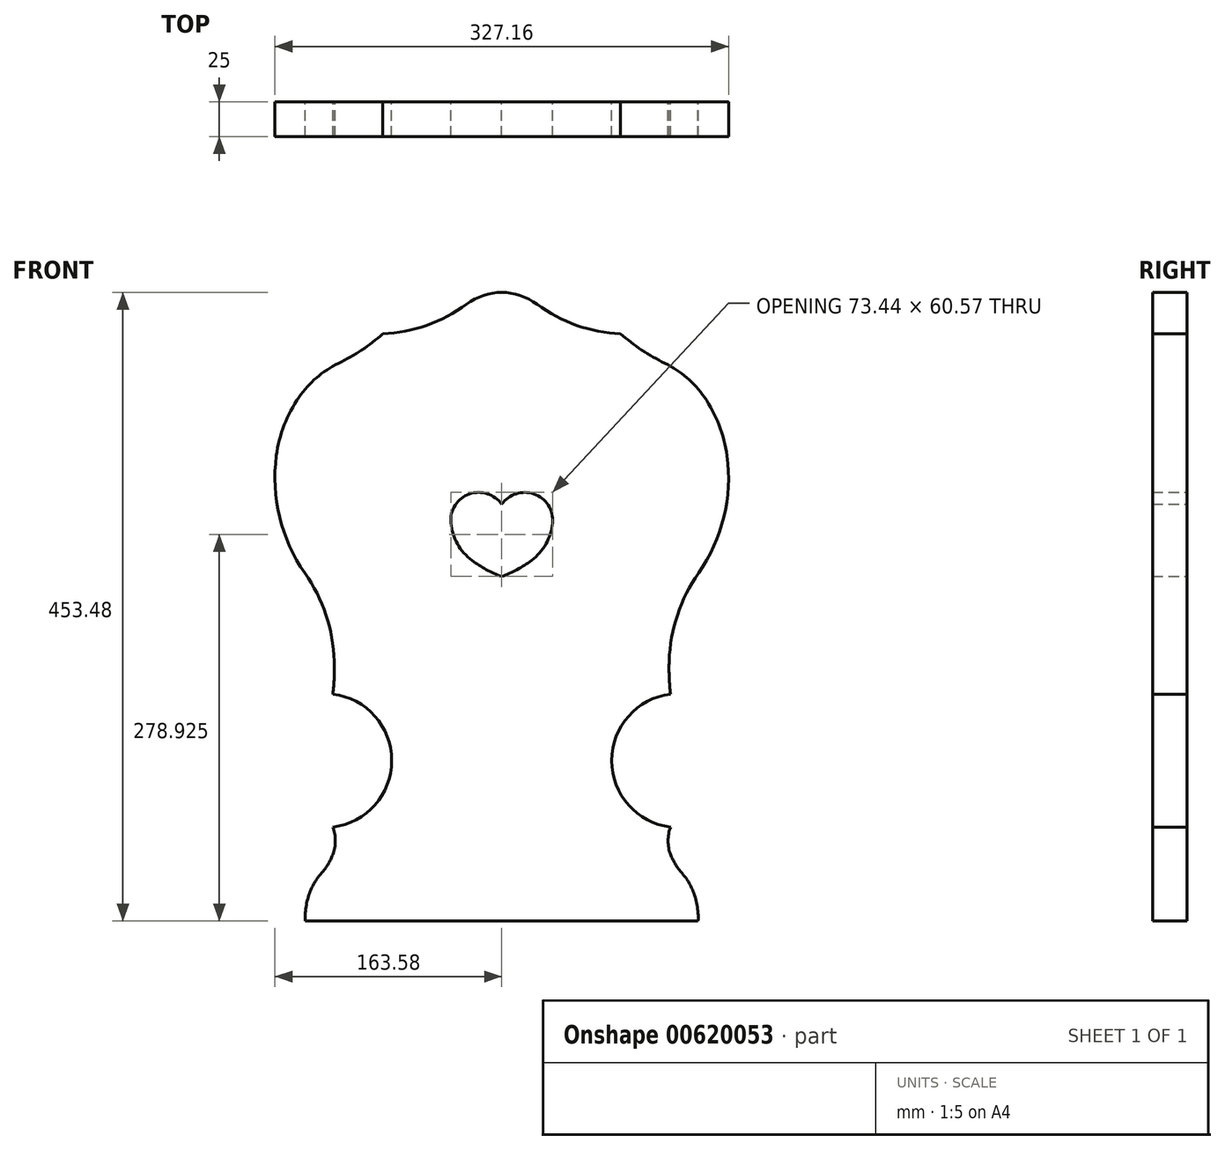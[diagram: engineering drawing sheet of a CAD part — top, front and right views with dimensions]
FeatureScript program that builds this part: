
annotation { "Feature Type Name" : "Feature", "Feature Type Description" : "" }
export const myFeature = defineFeature(function(context is Context, id is Id, definition is map)
    precondition{}
    {
        {
            var Q0;
            Q0=qCreatedBy(makeId("Front.planeOp"),FACE);
            var sketch = newSketch(context, id + "F0", { "sketchPlane" : qUnion([Q0])});
            skLineSegment(sketch, "E0", {"start": v(166.72, 456.5) * mm, "end": v(166.72, 0) * mm, "construction": true});
            skArc(sketch, "E1", {"start": v(81.01, 423.75) * mm, "mid": v(112.75, 429.77) * mm, "end": v(141.24, 445) * mm});
            skArc(sketch, "E2", {"start": v(4.2, 335.64) * mm, "mid": v(6.53, 291.46) * mm, "end": v(24.73, 251.14) * mm});
            skArc(sketch, "E3", {"start": v(24.73, 251.14) * mm, "mid": v(39.95, 220.9) * mm, "end": v(45.97, 187.6) * mm});
            skArc(sketch, "E4", {"start": v(45.97, 187.6) * mm, "mid": v(45.91, 175.63) * mm, "end": v(44.88, 163.7) * mm});
            skArc(sketch, "E5", {"start": v(44.88, 67.88) * mm, "mid": v(87.38, 115.8) * mm, "end": v(44.88, 163.7) * mm});
            skArc(sketch, "E6", {"start": v(4.2, 335.64) * mm, "mid": v(9.88, 357.82) * mm, "end": v(20.59, 378.06) * mm});
            skArc(sketch, "E7", {"start": v(20.59, 378.06) * mm, "mid": v(33.22, 392.07) * mm, "end": v(49, 402.4) * mm});
            skArc(sketch, "E8", {"start": v(49, 402.4) * mm, "mid": v(65.74, 411.97) * mm, "end": v(81.01, 423.75) * mm});
            skArc(sketch, "E9", {"start": v(44.88, 47.95) * mm, "mid": v(46.75, 57.92) * mm, "end": v(44.88, 67.88) * mm});
            skArc(sketch, "E10", {"start": v(44.88, 47.95) * mm, "mid": v(41.4, 40.9) * mm, "end": v(36.7, 34.58) * mm});
            skArc(sketch, "E11", {"start": v(36.7, 34.58) * mm, "mid": v(32.47, 29) * mm, "end": v(29.19, 22.8) * mm});
            skArc(sketch, "E12", {"start": v(29.19, 22.8) * mm, "mid": v(25.82, 11.64) * mm, "end": v(25.09, 0) * mm});
            skArc(sketch, "E13.MirrorCS", {"start": v(252.43, 423.75) * mm, "mid": v(220.7, 429.77) * mm, "end": v(192.2, 445) * mm});
            skArc(sketch, "E14.MirrorCS", {"start": v(284.44, 402.4) * mm, "mid": v(267.7, 411.97) * mm, "end": v(252.43, 423.75) * mm});
            skArc(sketch, "E15.MirrorCS", {"start": v(312.85, 378.06) * mm, "mid": v(300.22, 392.07) * mm, "end": v(284.44, 402.4) * mm});
            skArc(sketch, "E16.MirrorCS", {"start": v(329.25, 335.64) * mm, "mid": v(323.56, 357.82) * mm, "end": v(312.85, 378.06) * mm});
            skArc(sketch, "E17.MirrorCS", {"start": v(329.25, 335.64) * mm, "mid": v(326.91, 291.46) * mm, "end": v(308.7, 251.14) * mm});
            skArc(sketch, "E18.MirrorCS", {"start": v(308.7, 251.14) * mm, "mid": v(293.5, 220.9) * mm, "end": v(287.47, 187.6) * mm});
            skArc(sketch, "E19.MirrorCS", {"start": v(287.47, 187.6) * mm, "mid": v(287.53, 175.63) * mm, "end": v(288.56, 163.7) * mm});
            skArc(sketch, "E20.MirrorCS", {"start": v(288.56, 67.88) * mm, "mid": v(246.06, 115.8) * mm, "end": v(288.56, 163.7) * mm});
            skArc(sketch, "E21.MirrorCS", {"start": v(288.56, 47.95) * mm, "mid": v(286.7, 57.92) * mm, "end": v(288.56, 67.88) * mm});
            skArc(sketch, "E22.MirrorCS", {"start": v(288.56, 47.95) * mm, "mid": v(292.05, 40.9) * mm, "end": v(296.74, 34.58) * mm});
            skArc(sketch, "E23.MirrorCS", {"start": v(296.74, 34.58) * mm, "mid": v(300.97, 29) * mm, "end": v(304.25, 22.8) * mm});
            skArc(sketch, "E24.MirrorCS", {"start": v(304.25, 22.8) * mm, "mid": v(307.62, 11.64) * mm, "end": v(308.35, 0) * mm});
            skArc(sketch, "E25", {"start": v(189.92, 308.12) * mm, "mid": v(177.1, 308.25) * mm, "end": v(166.72, 300.74) * mm});
            skArc(sketch, "E26", {"start": v(189.92, 308.12) * mm, "mid": v(200.29, 300.03) * mm, "end": v(203.4, 287.25) * mm});
            skArc(sketch, "E27", {"start": v(203.4, 287.25) * mm, "mid": v(198.65, 272.1) * mm, "end": v(188.17, 260.17) * mm});
            skArc(sketch, "E28", {"start": v(188.17, 260.17) * mm, "mid": v(177.88, 253.6) * mm, "end": v(166.72, 248.64) * mm});
            skArc(sketch, "E29.MirrorCS", {"start": v(143.52, 308.12) * mm, "mid": v(156.34, 308.25) * mm, "end": v(166.72, 300.74) * mm});
            skArc(sketch, "E30.MirrorCS", {"start": v(143.52, 308.12) * mm, "mid": v(133.15, 300.03) * mm, "end": v(130.04, 287.25) * mm});
            skArc(sketch, "E31.MirrorCS", {"start": v(130.04, 287.25) * mm, "mid": v(134.8, 272.1) * mm, "end": v(145.27, 260.17) * mm});
            skArc(sketch, "E32.MirrorCS", {"start": v(145.27, 260.17) * mm, "mid": v(155.56, 253.6) * mm, "end": v(166.72, 248.64) * mm});
            skLineSegment(sketch, "E33", {"start": v(25.09, 0) * mm, "end": v(308.35, 0) * mm});
            skArc(sketch, "E34", {"start": v(141.24, 445) * mm, "mid": v(166.72, 453.48) * mm, "end": v(192.2, 445) * mm});
            skSolve(sketch);
        }
        {
            var Q0;
            Q0=makeQuery(id+"F0.imprint","IMPRINT",FACE,{"disambiguationData":[TD([[makeQuery(id+"F0.imprint","IMPRINT",EDGE,{"derivedFrom":sQuery(id+"F0.wireOp",EDGE,"E1")}),-1.0]])]});
            extrude(context, id + "F1", {"entities" : qUnion([Q0]), "depth" : 25 * mm, "offsetDistance" : 25 * mm});
        }
    });
